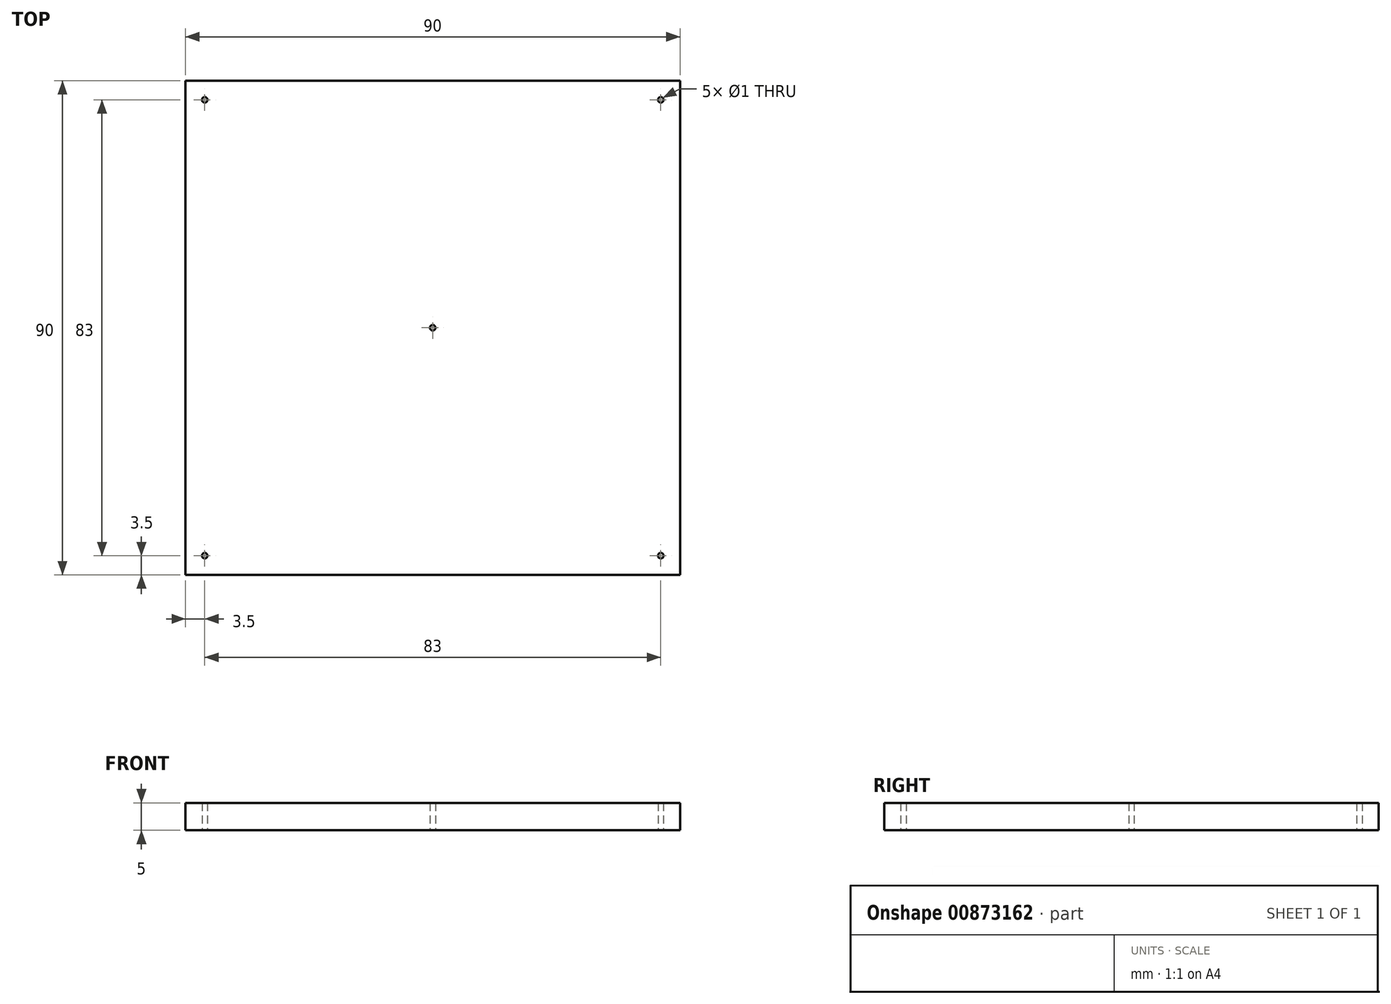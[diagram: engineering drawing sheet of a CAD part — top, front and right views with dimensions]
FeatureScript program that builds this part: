
annotation { "Feature Type Name" : "Feature", "Feature Type Description" : "" }
export const myFeature = defineFeature(function(context is Context, id is Id, definition is map)
    precondition{}
    {
        {
            var Q0;
            Q0=qCreatedBy(makeId("Top.planeOp"),FACE);
            var sketch = newSketch(context, id + "F0", { "sketchPlane" : qUnion([Q0])});
            skLineSegment(sketch, "E0.bottom", {"start": v(-45, 45) * mm, "end": v(45, 45) * mm});
            skLineSegment(sketch, "E0.top", {"start": v(-45, -45) * mm, "end": v(45, -45) * mm});
            skLineSegment(sketch, "E0.left", {"start": v(-45, 45) * mm, "end": v(-45, -45) * mm});
            skLineSegment(sketch, "E0.right", {"start": v(45, 45) * mm, "end": v(45, -45) * mm});
            skPoint(sketch, "E0.middle", {"position": v(0, 0) * mm});
            skLineSegment(sketch, "E1.bottom", {"start": v(41.5, 41.5) * mm, "end": v(-41.5, 41.5) * mm, "construction": true});
            skLineSegment(sketch, "E1.top", {"start": v(41.5, -41.5) * mm, "end": v(-41.5, -41.5) * mm, "construction": true});
            skLineSegment(sketch, "E1.left", {"start": v(41.5, 41.5) * mm, "end": v(41.5, -41.5) * mm, "construction": true});
            skLineSegment(sketch, "E1.right", {"start": v(-41.5, 41.5) * mm, "end": v(-41.5, -41.5) * mm, "construction": true});
            skCircle(sketch, "E2", {"center": v(-41.5, 41.5) * mm, "radius": 0.5 * mm});
            skCircle(sketch, "E3", {"center": v(41.5, 41.5) * mm, "radius": 0.5 * mm});
            skCircle(sketch, "E4", {"center": v(41.5, -41.5) * mm, "radius": 0.5 * mm});
            skCircle(sketch, "E5", {"center": v(-41.5, -41.5) * mm, "radius": 0.5 * mm});
            skCircle(sketch, "E6", {"center": v(0, 0) * mm, "radius": 0.5 * mm});
            skSolve(sketch);
        }
        {
            var Q0;
            Q0=makeQuery(id+"F0.imprint","IMPRINT",FACE,{"disambiguationData":[TD([[makeQuery(id+"F0.imprint","IMPRINT",EDGE,{"derivedFrom":sQuery(id+"F0.wireOp",EDGE,"E0.bottom")}),-1.0]])]});
            extrude(context, id + "F1", {"entities" : qUnion([Q0]), "depth" : 5 * mm, "offsetDistance" : 25 * mm});
        }
    });
